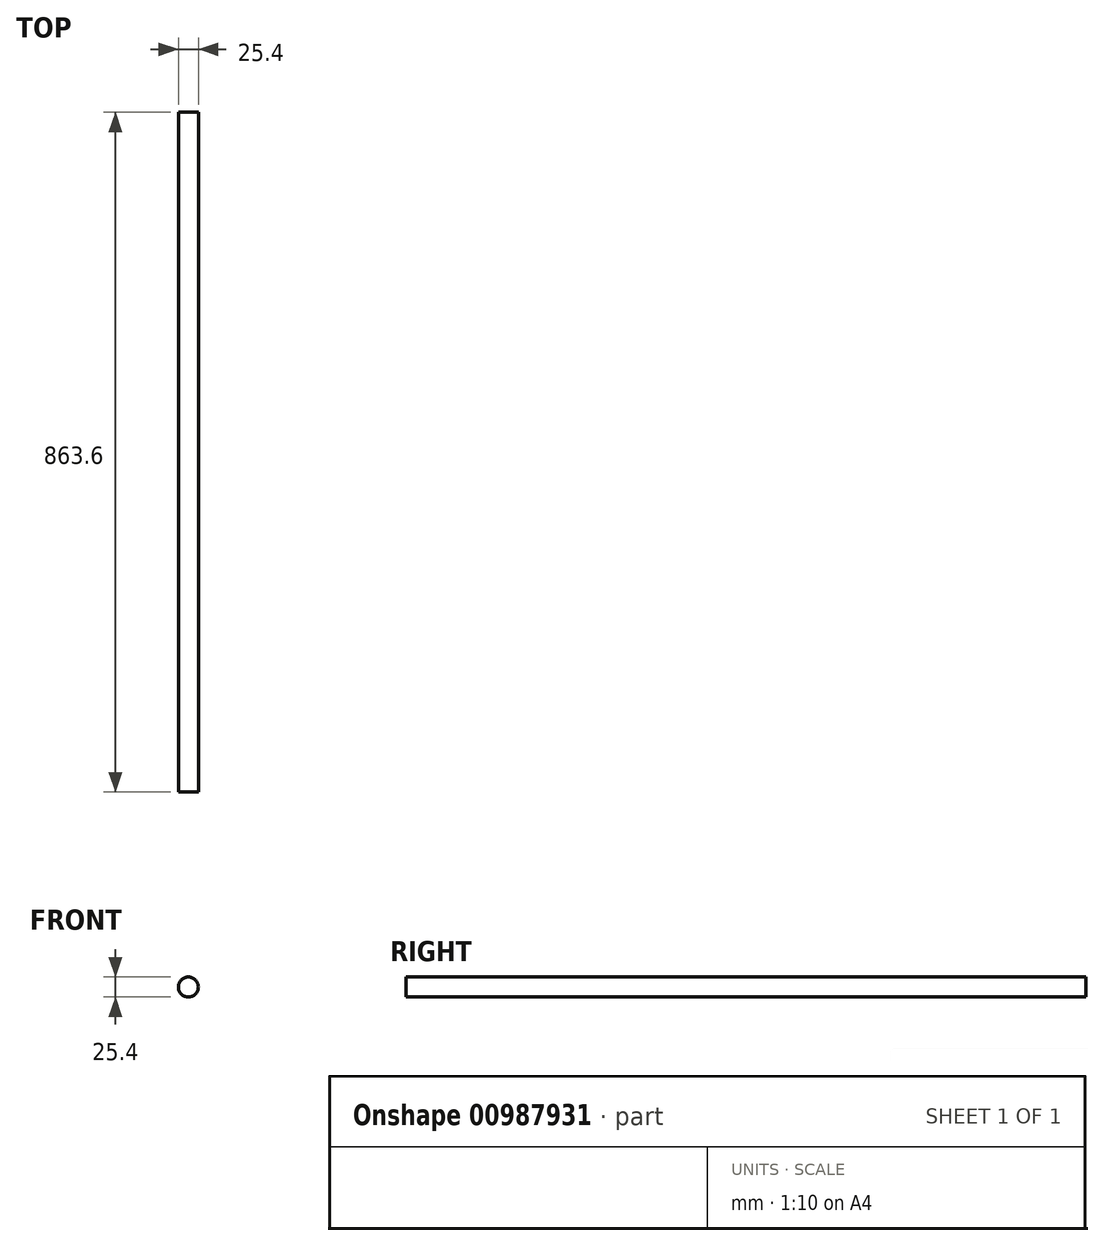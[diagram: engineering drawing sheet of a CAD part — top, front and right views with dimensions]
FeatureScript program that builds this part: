
annotation { "Feature Type Name" : "Feature", "Feature Type Description" : "" }
export const myFeature = defineFeature(function(context is Context, id is Id, definition is map)
    precondition{}
    {
        {
            var Q0;
            Q0=qCreatedBy(makeId("Front.planeOp"),FACE);
            var sketch = newSketch(context, id + "F0", { "sketchPlane" : qUnion([Q0])});
            skCircle(sketch, "E0", {"center": v(0, 0) * mm, "radius": 12.7 * mm});
            skSolve(sketch);
        }
        {
            var Q0;
            Q0=makeQuery(id+"F0.imprint","IMPRINT",FACE,{"disambiguationData":[TD([[makeQuery(id+"F0.imprint","IMPRINT",EDGE,{"derivedFrom":sQuery(id+"F0.wireOp",EDGE,"E0")}),1.0]])]});
            extrude(context, id + "F1", {"entities" : qUnion([Q0]), "depth" : 863.6 * mm, "offsetDistance" : 25.4 * mm});
        }
    });
